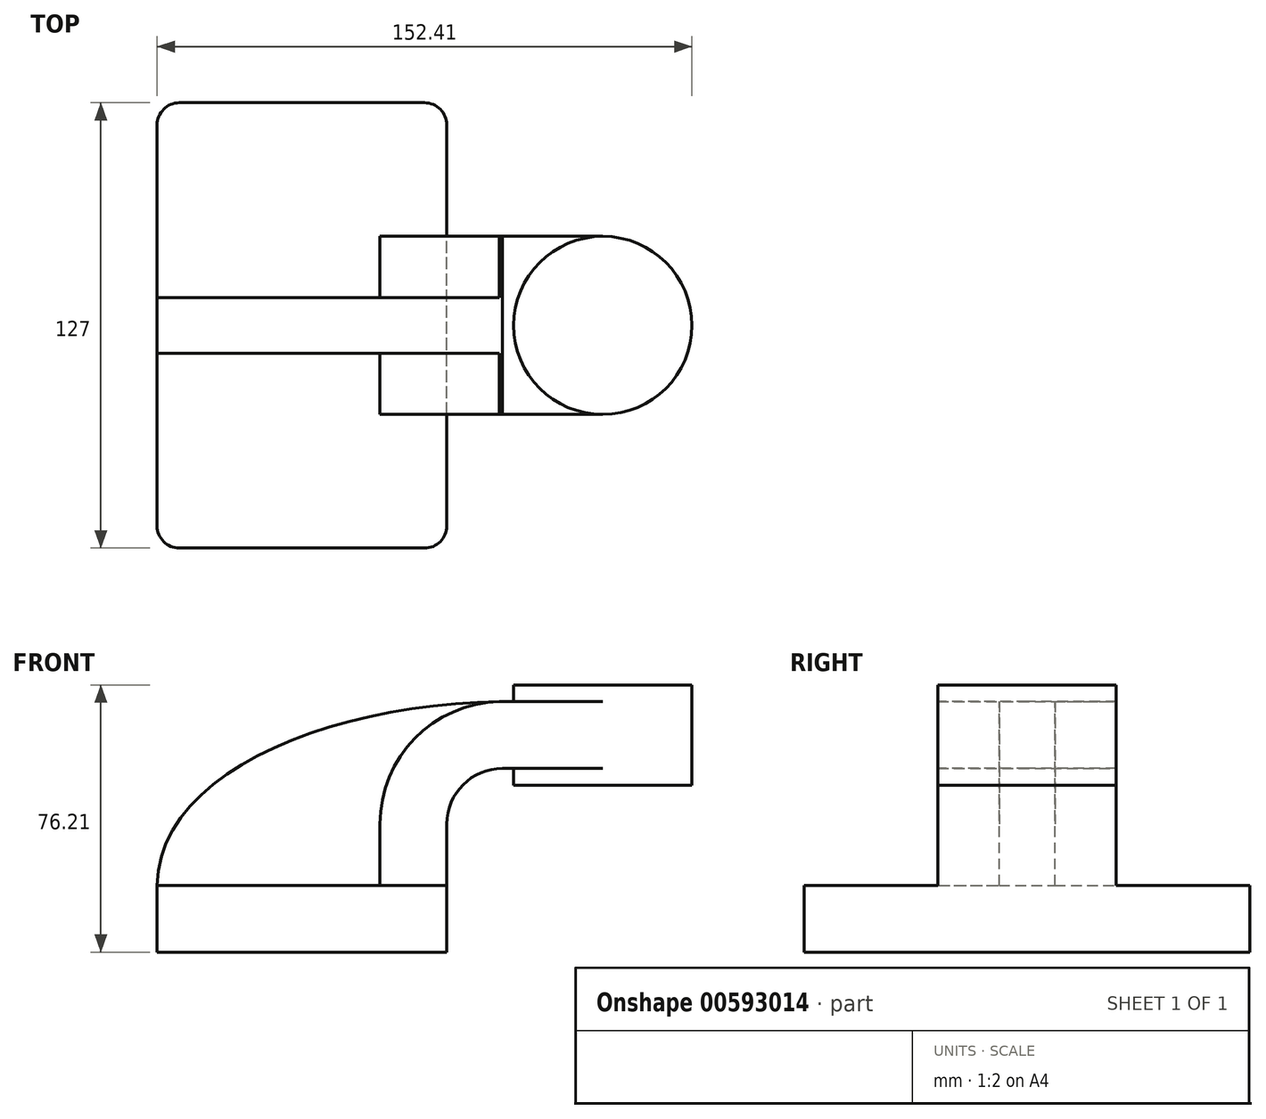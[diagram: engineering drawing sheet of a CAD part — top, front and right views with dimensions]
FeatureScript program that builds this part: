
annotation { "Feature Type Name" : "Feature", "Feature Type Description" : "" }
export const myFeature = defineFeature(function(context is Context, id is Id, definition is map)
    precondition{}
    {
        {
            var Q0;
            Q0=qCreatedBy(makeId("Front.planeOp"),FACE);
            var sketch = newSketch(context, id + "F0", { "sketchPlane" : qUnion([Q0])});
            skLineSegment(sketch, "E0.bottom", {"start": v(-41.27, -9.53) * mm, "end": v(41.28, -9.53) * mm});
            skLineSegment(sketch, "E0.top", {"start": v(-41.28, 9.52) * mm, "end": v(41.28, 9.52) * mm});
            skLineSegment(sketch, "E0.left", {"start": v(-41.28, -9.53) * mm, "end": v(-41.28, 9.52) * mm});
            skLineSegment(sketch, "E0.right", {"start": v(41.28, -9.53) * mm, "end": v(41.28, 9.52) * mm});
            skPoint(sketch, "E0.middle", {"position": v(0, 0) * mm});
            skLineSegment(sketch, "E1.bottom", {"start": v(111.13, 38.1) * mm, "end": v(60.32, 38.1) * mm});
            skLineSegment(sketch, "E1.top", {"start": v(111.13, 66.67) * mm, "end": v(60.33, 66.67) * mm});
            skLineSegment(sketch, "E1.left", {"start": v(111.13, 38.1) * mm, "end": v(111.13, 66.67) * mm});
            skLineSegment(sketch, "E1.right", {"start": v(60.33, 38.1) * mm, "end": v(60.33, 66.67) * mm});
            skPoint(sketch, "E1.middle", {"position": v(85.73, 52.39) * mm});
            skLineSegment(sketch, "E2", {"start": v(41.28, 9.52) * mm, "end": v(41.28, 26.99) * mm});
            skArc(sketch, "E3", {"start": v(41.27, 26.99) * mm, "mid": v(45.92, 38.21) * mm, "end": v(57.15, 42.86) * mm});
            skLineSegment(sketch, "E4", {"start": v(57.15, 42.86) * mm, "end": v(85.73, 42.86) * mm});
            skLineSegment(sketch, "E5.0", {"start": v(57.15, 61.91) * mm, "end": v(85.73, 61.91) * mm});
            skArc(sketch, "E5.1", {"start": v(22.22, 26.99) * mm, "mid": v(32.45, 51.68) * mm, "end": v(57.15, 61.91) * mm});
            skLineSegment(sketch, "E5.2", {"start": v(22.22, 9.52) * mm, "end": v(22.22, 26.99) * mm});
            skLineSegment(sketch, "E6", {"start": v(85.73, 38.1) * mm, "end": v(85.73, 66.67) * mm});
            skFitSpline(sketch, "E7", {"points": [v(-41.27, 9.53) * mm, v(57.15, 61.91) * mm], "startDerivative": vector(1.51, 97.8) * mm, "endDerivative": vector(145.44, 1.48) * mm});
            skSolve(sketch);
        }
        {
            var Q0;
            Q0=makeQuery(id+"F0.imprint","IMPRINT",FACE,{"disambiguationData":[TD([[makeQuery(id+"F0.imprint","IMPRINT",EDGE,{"derivedFrom":sQuery(id+"F0.wireOp",EDGE,"E0.bottom")}),1.0]])]});
            extrude(context, id + "F1", {"entities" : qUnion([Q0]), "endBound" : BoundingType.SYMMETRIC, "depth" : 127 * mm, "offsetDistance" : 25.4 * mm});
        }
        {
            var Q0;
            {var subQ1=sQuery(id+"F0.wireOp",EDGE,"E2");Q0=makeQuery(id+"F0.imprint","IMPRINT",FACE,{"disambiguationData":[TD([[makeQuery(id+"F0.imprint","IMPRINT",EDGE,{"derivedFrom":subQ1}),1.0]])]});}
            var Q1;
            {var subQ0=sQuery(id+"F0.wireOp",EDGE,"E4");var subQ1=sQuery(id+"F0.wireOp",EDGE,"E1.right");var subQ2=makeQuery(id+"F0.imprint","INTERSECT",VERTEX,{"derivedFrom":[subQ1,subQ0]});Q1=makeQuery(id+"F0.imprint","IMPRINT",FACE,{"disambiguationData":[TD([[makeQuery(id+"F0.imprint","IMPRINT",EDGE,{"disambiguationData":[TD([[subQ2,-1.0]])],"derivedFrom":subQ1}),-1.0]])]});}
            extrude(context, id + "F2", {"entities" : qUnion([Q0, Q1]), "operationType" : NewBodyOperationType.ADD, "endBound" : BoundingType.SYMMETRIC, "depth" : 50.8 * mm, "offsetDistance" : 25.4 * mm});
        }
        {
            var Q0;
            {var subQ3=sQuery(id+"F0.wireOp",EDGE,"E5.2");Q0=makeQuery(id+"F0.imprint","IMPRINT",FACE,{"disambiguationData":[TD([[makeQuery(id+"F0.imprint","IMPRINT",EDGE,{"derivedFrom":subQ3}),1.0]])]});}
            extrude(context, id + "F3", {"entities" : qUnion([Q0]), "operationType" : NewBodyOperationType.ADD, "endBound" : BoundingType.SYMMETRIC, "depth" : 15.88 * mm, "offsetDistance" : 25.4 * mm});
        }
        {
            var Q0;
            {var subQ0=sQuery(id+"F0.wireOp",EDGE,"E1.left");Q0=makeQuery(id+"F0.imprint","IMPRINT",FACE,{"disambiguationData":[TD([[makeQuery(id+"F0.imprint","IMPRINT",EDGE,{"derivedFrom":subQ0}),1.0]])]});}
            var Q1;
            Q1=sQuery(id+"F0.wireOp",EDGE,"E6");
            revolve(context, id + "F4", {"operationType" : NewBodyOperationType.ADD, "entities" : qUnion([Q0]), "axis" : qUnion([Q1]), "revolveType" : RevolveType.FULL});
        }
        {
            var Q0;
            Q0=makeQuery(id+"F1.opExtrude","CAP_EDGE",EDGE,{"disambiguationData":[OSD([sQuery(id+"F0.wireOp",EDGE,"E0.left")])],"isStart":false});
            var Q1;
            Q1=makeQuery(id+"F1.opExtrude","CAP_EDGE",EDGE,{"disambiguationData":[OSD([sQuery(id+"F0.wireOp",EDGE,"E0.right")])],"isStart":false});
            var Q2;
            Q2=makeQuery(id+"F1.opExtrude","CAP_EDGE",EDGE,{"disambiguationData":[OSD([sQuery(id+"F0.wireOp",EDGE,"E0.right")])],"isStart":true});
            var Q3;
            Q3=makeQuery(id+"F1.opExtrude","CAP_EDGE",EDGE,{"disambiguationData":[OSD([sQuery(id+"F0.wireOp",EDGE,"E0.left")])],"isStart":true});
            fillet(context, id + "F5", {"entities" : qUnion([Q0, Q1, Q2, Q3]), "radius" : 6.35 * mm, "tangentPropagation" : true, "allowEdgeOverflow" : false});
        }
    });
